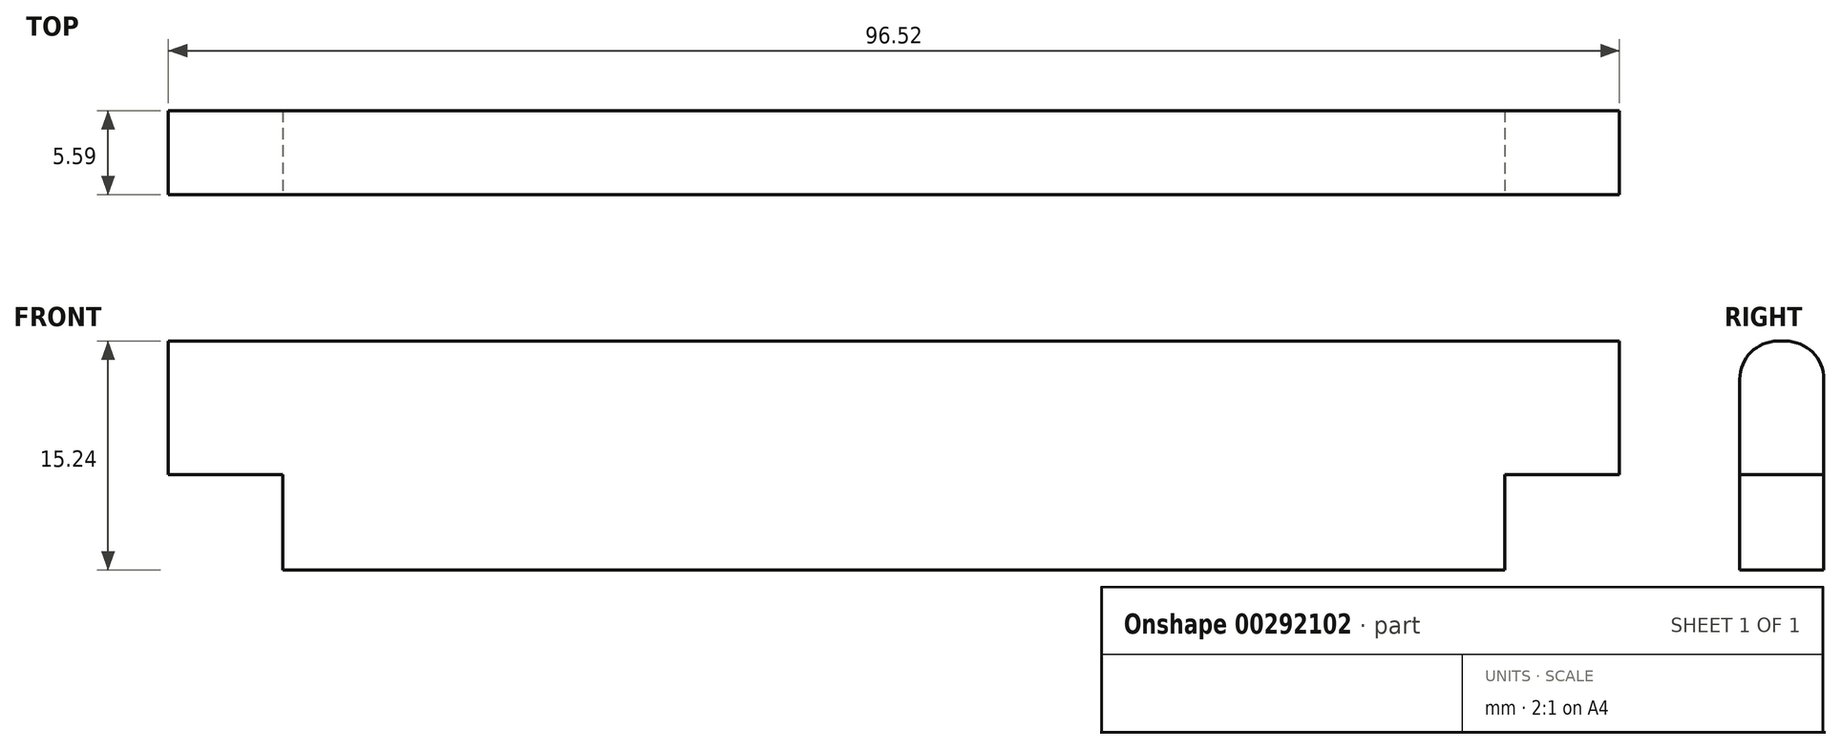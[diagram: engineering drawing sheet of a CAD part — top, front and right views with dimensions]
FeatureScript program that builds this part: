
annotation { "Feature Type Name" : "Feature", "Feature Type Description" : "" }
export const myFeature = defineFeature(function(context is Context, id is Id, definition is map)
    precondition{}
    {
        {
            var Q0;
            Q0=qCreatedBy(makeId("Front.planeOp"),FACE);
            var sketch = newSketch(context, id + "F0", { "sketchPlane" : qUnion([Q0])});
            skLineSegment(sketch, "E0.bottom", {"start": v(0, 0) * mm, "end": v(96.52, 0) * mm});
            skLineSegment(sketch, "E0.top", {"start": v(0, -15.24) * mm, "end": v(96.52, -15.24) * mm});
            skLineSegment(sketch, "E0.left", {"start": v(0, 0) * mm, "end": v(0, -15.24) * mm});
            skLineSegment(sketch, "E0.right", {"start": v(96.52, 0) * mm, "end": v(96.52, -15.24) * mm});
            skSolve(sketch);
        }
        {
            var Q0;
            Q0 = qSketchRegion(id + "F0", true);
            extrude(context, id + "F1", {"entities" : qUnion([Q0]), "depth" : 5.6 * mm});
        }
        {
            var Q0;
            Q0=makeQuery(id+"F1.opExtrude","CAP_FACE",FACE,{"disambiguationData":[OSD([sQuery(id+"F0.wireOp",EDGE,"E0.bottom"),sQuery(id+"F0.wireOp",EDGE,"E0.top"),sQuery(id+"F0.wireOp",EDGE,"E0.left"),sQuery(id+"F0.wireOp",EDGE,"E0.right")])],"isStart":false});
            var sketch = newSketch(context, id + "F2", { "sketchPlane" : qUnion([Q0])});
            skLineSegment(sketch, "E1.bottom", {"start": v(96.52, -15.24) * mm, "end": v(88.9, -15.24) * mm});
            skLineSegment(sketch, "E1.top", {"start": v(96.52, -8.9) * mm, "end": v(88.9, -8.9) * mm});
            skLineSegment(sketch, "E1.left", {"start": v(96.52, -15.24) * mm, "end": v(96.52, -8.9) * mm});
            skLineSegment(sketch, "E1.right", {"start": v(88.9, -15.24) * mm, "end": v(88.9, -8.9) * mm});
            skLineSegment(sketch, "E2.bottom", {"start": v(0, -15.24) * mm, "end": v(7.62, -15.24) * mm});
            skLineSegment(sketch, "E2.top", {"start": v(0, -8.9) * mm, "end": v(7.62, -8.9) * mm});
            skLineSegment(sketch, "E2.left", {"start": v(0, -15.24) * mm, "end": v(0, -8.9) * mm});
            skLineSegment(sketch, "E2.right", {"start": v(7.62, -15.24) * mm, "end": v(7.62, -8.9) * mm});
            skSolve(sketch);
        }
        {
            var Q0;
            Q0 = qSketchRegion(id + "F2", true);
            extrude(context, id + "F3", {"entities" : qUnion([Q0]), "operationType" : NewBodyOperationType.REMOVE, "oppositeDirection" : true, "depth" : 25.4 * mm});
        }
        {
            var Q0;
            Q0=makeQuery(id+"F1.opExtrude","CAP_EDGE",EDGE,{"disambiguationData":[OSD([sQuery(id+"F0.wireOp",EDGE,"E0.bottom")])],"isStart":true});
            var Q1;
            Q1=makeQuery(id+"F1.opExtrude","CAP_EDGE",EDGE,{"disambiguationData":[OSD([sQuery(id+"F0.wireOp",EDGE,"E0.bottom")])],"isStart":false});
            fillet(context, id + "F4", {"entities" : qUnion([Q0, Q1]), "radius" : 2.54 * mm, "allowEdgeOverflow" : false});
        }
    });
